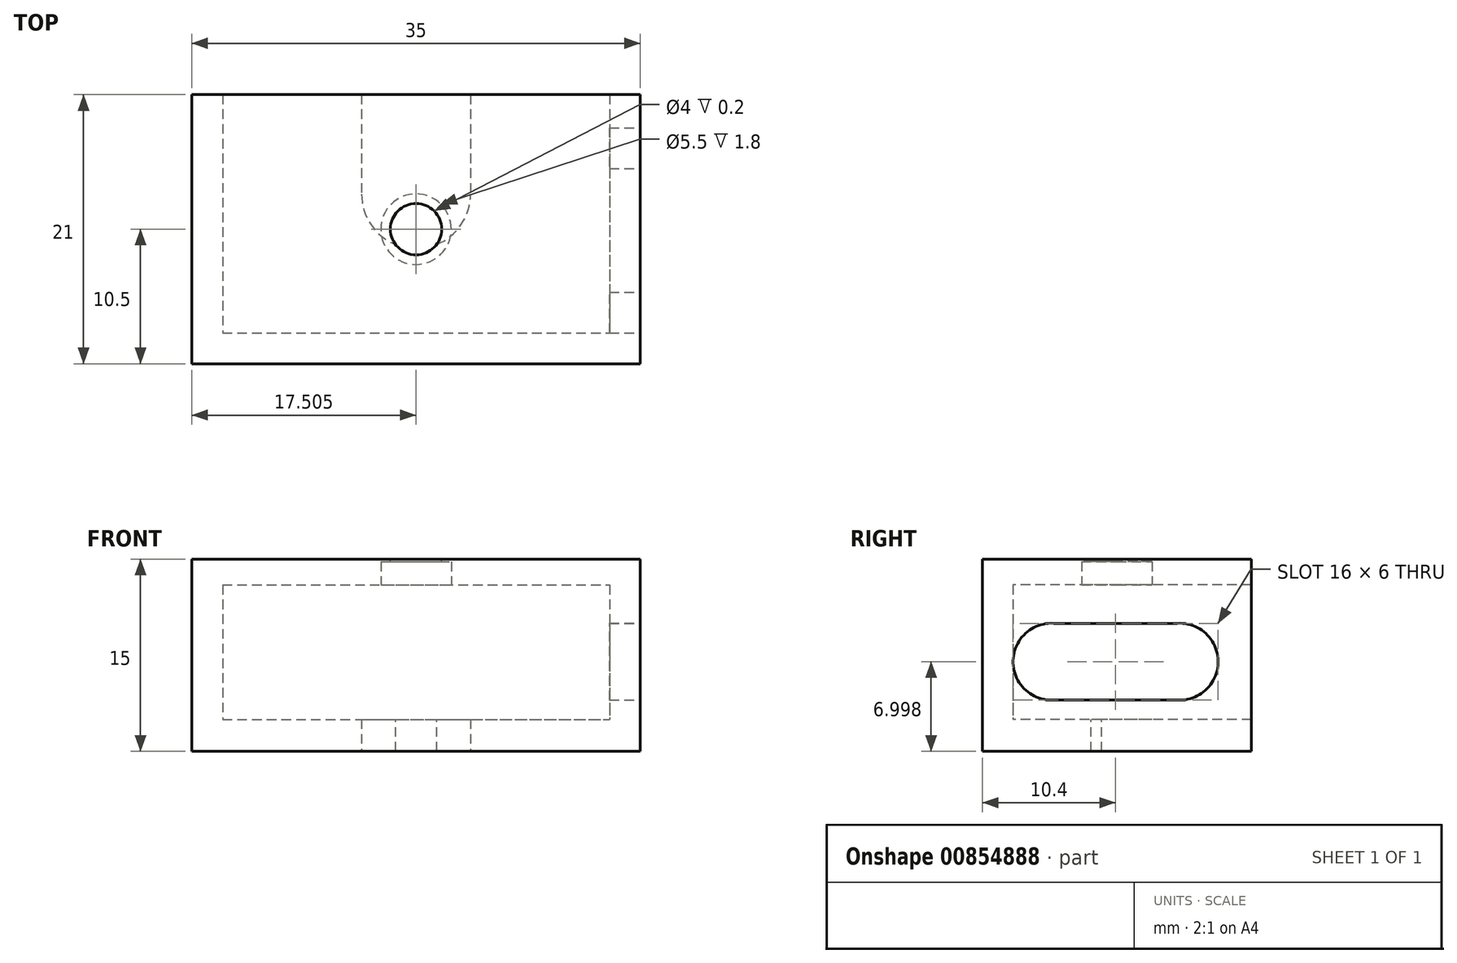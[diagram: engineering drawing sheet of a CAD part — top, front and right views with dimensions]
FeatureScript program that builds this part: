
annotation { "Feature Type Name" : "Feature", "Feature Type Description" : "" }
export const myFeature = defineFeature(function(context is Context, id is Id, definition is map)
    precondition{}
    {
        {
            var Q0;
            Q0=qCreatedBy(makeId("Top.planeOp"),FACE);
            var sketch = newSketch(context, id + "F0", { "sketchPlane" : qUnion([Q0])});
            skLineSegment(sketch, "E0.bottom", {"start": v(-12.39, 5.77) * mm, "end": v(0.86, 5.77) * mm});
            skLineSegment(sketch, "E0.top", {"start": v(-12.39, -15.23) * mm, "end": v(22.61, -15.23) * mm});
            skLineSegment(sketch, "E0.left", {"start": v(-12.39, 5.77) * mm, "end": v(-12.39, -15.23) * mm});
            skLineSegment(sketch, "E0.right", {"start": v(22.61, 5.77) * mm, "end": v(22.61, -15.23) * mm});
            skLineSegment(sketch, "E1.left", {"start": v(0.86, 5.77) * mm, "end": v(0.86, -1.99) * mm});
            skLineSegment(sketch, "E1.right", {"start": v(9.36, 5.77) * mm, "end": v(9.36, -1.99) * mm});
            skPoint(sketch, "E2", {"position": v(5.11, 5.77) * mm});
            skPoint(sketch, "E3", {"position": v(5.11, -1.99) * mm});
            skArc(sketch, "E4", {"start": v(0.86, -1.99) * mm, "mid": v(5.11, -6.24) * mm, "end": v(9.36, -1.99) * mm});
            skLineSegment(sketch, "E5.trimOffspring", {"start": v(9.36, 5.77) * mm, "end": v(22.61, 5.77) * mm});
            skSolve(sketch);
        }
        {
            var Q0;
            Q0 = qSketchRegion(id + "F0", true);
            extrude(context, id + "F1", {"entities" : qUnion([Q0]), "depth" : 2.5 * mm, "offsetDistance" : 25 * mm});
        }
        {
            var Q0;
            Q0=makeQuery(id+"F1.opExtrude","CAP_FACE",FACE,{"disambiguationData":[OSD([sQuery(id+"F0.wireOp",EDGE,"E0.bottom"),sQuery(id+"F0.wireOp",EDGE,"E0.top"),sQuery(id+"F0.wireOp",EDGE,"E0.left"),sQuery(id+"F0.wireOp",EDGE,"E0.right"),sQuery(id+"F0.wireOp",EDGE,"E1.left"),sQuery(id+"F0.wireOp",EDGE,"E1.right"),sQuery(id+"F0.wireOp",EDGE,"E4"),sQuery(id+"F0.wireOp",EDGE,"E5.trimOffspring")])],"isStart":false});
            var sketch = newSketch(context, id + "F2", { "sketchPlane" : qUnion([Q0])});
            skLineSegment(sketch, "E6.bottom", {"start": v(-12.39, 5.77) * mm, "end": v(-9.99, 5.77) * mm});
            skLineSegment(sketch, "E6.top", {"start": v(-12.39, -15.23) * mm, "end": v(22.61, -15.23) * mm});
            skLineSegment(sketch, "E6.left", {"start": v(-12.39, 5.77) * mm, "end": v(-12.39, -15.23) * mm});
            skLineSegment(sketch, "E6.right", {"start": v(22.61, 5.77) * mm, "end": v(22.61, -15.23) * mm});
            skLineSegment(sketch, "E7.top", {"start": v(-9.99, -12.83) * mm, "end": v(20.21, -12.83) * mm});
            skLineSegment(sketch, "E7.left", {"start": v(-9.99, 5.77) * mm, "end": v(-9.99, -12.83) * mm});
            skLineSegment(sketch, "E7.right", {"start": v(20.21, 5.77) * mm, "end": v(20.21, -12.83) * mm});
            skLineSegment(sketch, "E8.trimOffspring", {"start": v(20.21, 5.77) * mm, "end": v(22.61, 5.77) * mm});
            skSolve(sketch);
        }
        {
            var Q0;
            Q0 = qSketchRegion(id + "F2", true);
            extrude(context, id + "F3", {"entities" : qUnion([Q0]), "operationType" : NewBodyOperationType.ADD, "depth" : 10.5 * mm, "offsetDistance" : 25 * mm});
        }
        {
            var Q0;
            Q0=makeQuery(id+"F3.opExtrude","CAP_FACE",FACE,{"disambiguationData":[OSD([sQuery(id+"F2.wireOp",EDGE,"E6.bottom"),sQuery(id+"F2.wireOp",EDGE,"E6.top"),sQuery(id+"F2.wireOp",EDGE,"E6.left"),sQuery(id+"F2.wireOp",EDGE,"E6.right"),sQuery(id+"F2.wireOp",EDGE,"E7.top"),sQuery(id+"F2.wireOp",EDGE,"E7.left"),sQuery(id+"F2.wireOp",EDGE,"E7.right"),sQuery(id+"F2.wireOp",EDGE,"E8.trimOffspring")])],"isStart":false});
            var sketch = newSketch(context, id + "F4", { "sketchPlane" : qUnion([Q0])});
            skLineSegment(sketch, "E9.bottom", {"start": v(-12.39, 5.77) * mm, "end": v(22.61, 5.77) * mm});
            skLineSegment(sketch, "E9.top", {"start": v(-12.39, -15.23) * mm, "end": v(22.61, -15.23) * mm});
            skLineSegment(sketch, "E9.left", {"start": v(-12.39, 5.77) * mm, "end": v(-12.39, -15.23) * mm});
            skLineSegment(sketch, "E9.right", {"start": v(22.61, 5.77) * mm, "end": v(22.61, -15.23) * mm});
            skSolve(sketch);
        }
        {
            var Q0;
            Q0 = qSketchRegion(id + "F4", true);
            extrude(context, id + "F5", {"entities" : qUnion([Q0]), "operationType" : NewBodyOperationType.ADD, "depth" : 2 * mm, "offsetDistance" : 25 * mm});
        }
        {
            var Q0;
            Q0=makeQuery(id+"F5.boolean.opBoolean","MERGE",FACE,{"derivedFrom":[makeQuery(id+"F3.boolean.opBoolean","MERGE",FACE,{"derivedFrom":[makeQuery(id+"F1.opExtrude","SWEPT_FACE",FACE,{"disambiguationData":[OSD([sQuery(id+"F0.wireOp",EDGE,"E0.right")])]}),makeQuery(id+"F3.opExtrude","SWEPT_FACE",FACE,{"disambiguationData":[OSD([sQuery(id+"F2.wireOp",EDGE,"E6.right")])]})]}),makeQuery(id+"F5.opExtrude","SWEPT_FACE",FACE,{"disambiguationData":[OSD([sQuery(id+"F4.wireOp",EDGE,"E9.right")])]})]});
            var sketch = newSketch(context, id + "F6", { "sketchPlane" : qUnion([Q0])});
            skPoint(sketch, "E10.centerSnap0", {"position": v(5.77, 7.5) * mm});
            skLineSegment(sketch, "E11.0", {"start": v(0.17, 7) * mm, "end": v(-15.23, 7) * mm, "construction": true});
            skLineSegment(sketch, "E12.0", {"start": v(-9.83, 7) * mm, "end": v(-9.83, 0) * mm, "construction": true});
            skLineSegment(sketch, "E13.0", {"start": v(0.17, 7) * mm, "end": v(0.17, 0) * mm, "construction": true});
            skArc(sketch, "E14", {"start": v(0.17, 4) * mm, "mid": v(3.17, 7.08) * mm, "end": v(0, 10) * mm});
            skArc(sketch, "E15", {"start": v(-9.66, 10) * mm, "mid": v(-12.83, 7.08) * mm, "end": v(-9.83, 4) * mm});
            skLineSegment(sketch, "E16", {"start": v(0.17, 4) * mm, "end": v(-9.83, 4) * mm});
            skLineSegment(sketch, "E17", {"start": v(0, 10) * mm, "end": v(-9.66, 10) * mm});
            skSolve(sketch);
        }
        {
            var Q0;
            Q0 = qSketchRegion(id + "F6", true);
            extrude(context, id + "F7", {"entities" : qUnion([Q0]), "operationType" : NewBodyOperationType.REMOVE, "oppositeDirection" : true, "depth" : 2.4 * mm, "offsetDistance" : 25 * mm});
        }
        {
            var Q0;
            Q0=makeQuery(id+"F5.opExtrude","CAP_FACE",FACE,{"disambiguationData":[OSD([sQuery(id+"F4.wireOp",EDGE,"E9.bottom"),sQuery(id+"F4.wireOp",EDGE,"E9.top"),sQuery(id+"F4.wireOp",EDGE,"E9.left"),sQuery(id+"F4.wireOp",EDGE,"E9.right")])],"isStart":false});
            var sketch = newSketch(context, id + "F8", { "sketchPlane" : qUnion([Q0])});
            skLineSegment(sketch, "E18", {"start": v(5.11, 5.77) * mm, "end": v(5.11, -4.73) * mm, "construction": true});
            skLineSegment(sketch, "E19", {"start": v(-12.39, -4.73) * mm, "end": v(5.11, -4.73) * mm, "construction": true});
            skPoint(sketch, "E20.orphan", {"position": v(22.61, -4.73) * mm});
            skPoint(sketch, "E21.orphan", {"position": v(5.11, -15.23) * mm});
            skCircle(sketch, "E22", {"center": v(5.11, -4.73) * mm, "radius": 2 * mm});
            skSolve(sketch);
        }
        {
            var Q0;
            Q0 = qSketchRegion(id + "F8", true);
            extrude(context, id + "F9", {"entities" : qUnion([Q0]), "operationType" : NewBodyOperationType.REMOVE, "oppositeDirection" : true, "depth" : 25 * mm, "offsetDistance" : 25 * mm});
        }
        {
            var Q0;
            Q0=makeQuery(id+"F5.opExtrude","CAP_FACE",FACE,{"disambiguationData":[OSD([sQuery(id+"F4.wireOp",EDGE,"E9.bottom"),sQuery(id+"F4.wireOp",EDGE,"E9.top"),sQuery(id+"F4.wireOp",EDGE,"E9.left"),sQuery(id+"F4.wireOp",EDGE,"E9.right")])],"isStart":true});
            var sketch = newSketch(context, id + "F10", { "sketchPlane" : qUnion([Q0])});
            skCircle(sketch, "E23", {"center": v(5.11, 4.73) * mm, "radius": 2.75 * mm});
            skSolve(sketch);
        }
        {
            var Q0;
            Q0 = qSketchRegion(id + "F10", true);
            extrude(context, id + "F11", {"entities" : qUnion([Q0]), "operationType" : NewBodyOperationType.REMOVE, "oppositeDirection" : true, "depth" : 1.8 * mm, "offsetDistance" : 25 * mm});
        }
    });
